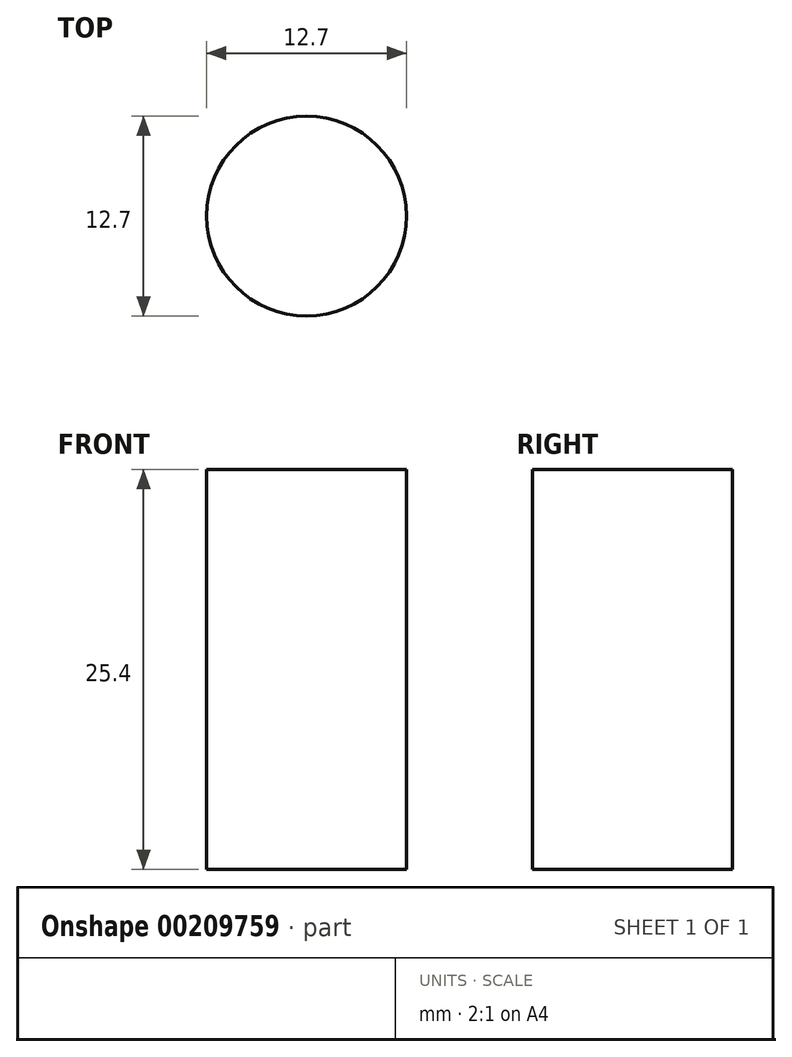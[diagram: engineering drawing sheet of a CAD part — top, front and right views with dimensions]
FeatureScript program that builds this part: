
annotation { "Feature Type Name" : "Feature", "Feature Type Description" : "" }
export const myFeature = defineFeature(function(context is Context, id is Id, definition is map)
    precondition{}
    {
        {
            var Q0;
            Q0=qCreatedBy(makeId("Front.planeOp"),FACE);
            var sketch = newSketch(context, id + "F0", { "sketchPlane" : qUnion([Q0])});
            skLineSegment(sketch, "E0.bottom", {"start": v(0, 0) * mm, "end": v(6.35, 0) * mm});
            skLineSegment(sketch, "E0.top", {"start": v(0, 25.4) * mm, "end": v(6.35, 25.4) * mm});
            skLineSegment(sketch, "E0.left", {"start": v(0, 0) * mm, "end": v(0, 25.4) * mm});
            skLineSegment(sketch, "E0.right", {"start": v(6.35, 0) * mm, "end": v(6.35, 25.4) * mm});
            skSolve(sketch);
        }
        {
            var Q0;
            Q0 = qSketchRegion(id + "F0", true);
            var Q1;
            Q1=sQuery(id+"F0.wireOp",EDGE,"E0.left");
            revolve(context, id + "F1", {"entities" : qUnion([Q0]), "axis" : qUnion([Q1]), "revolveType" : RevolveType.FULL});
        }
    });
